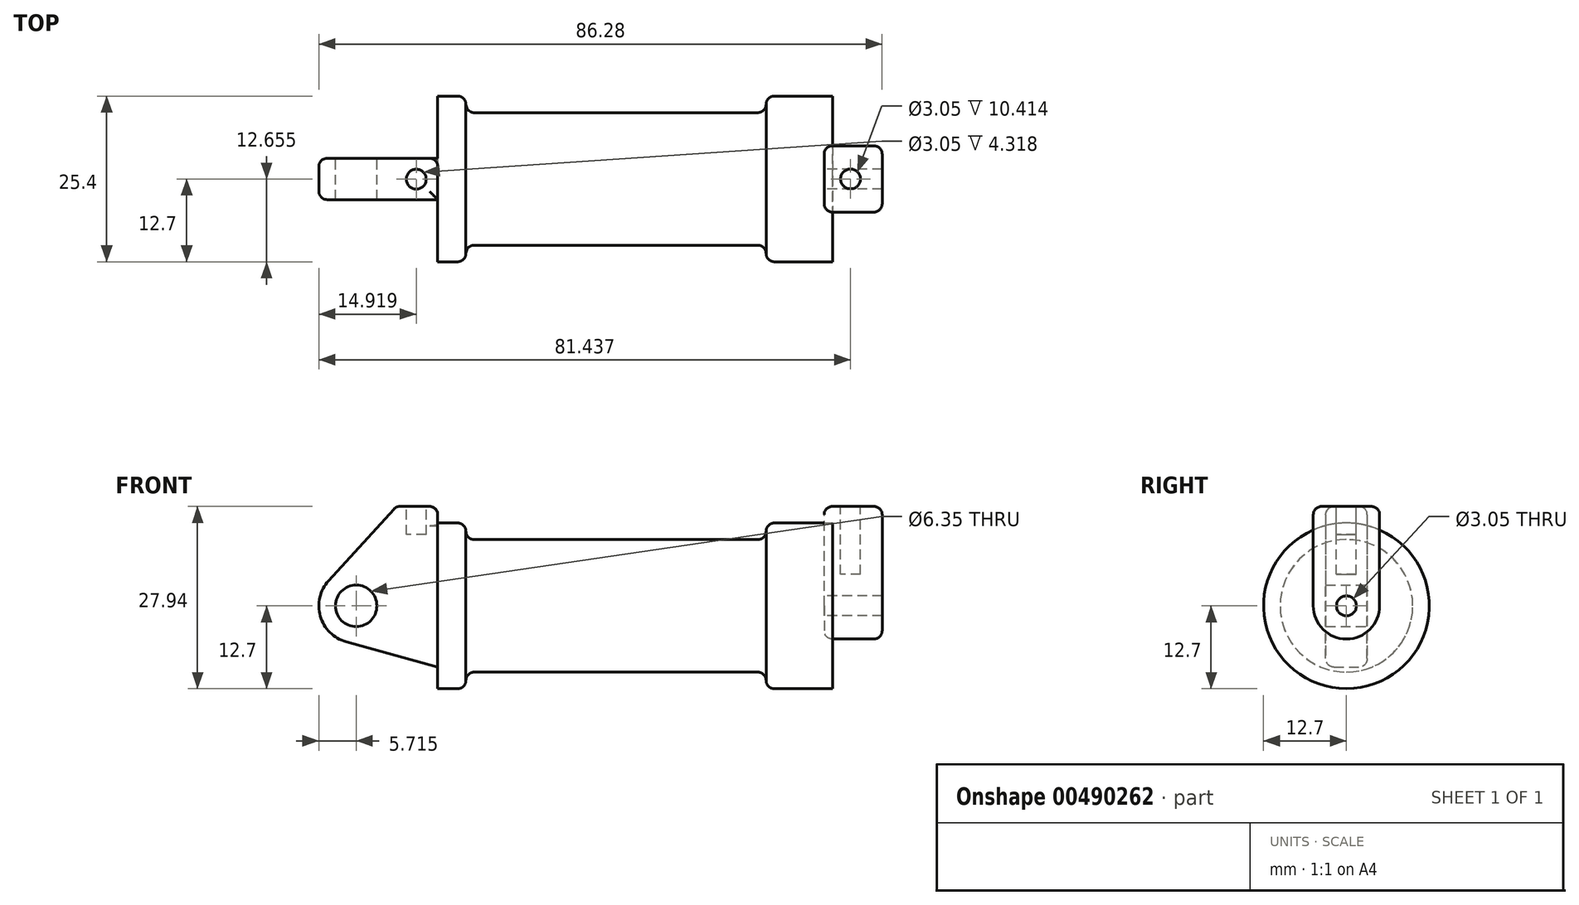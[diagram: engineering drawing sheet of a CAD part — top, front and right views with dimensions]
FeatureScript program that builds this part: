
annotation { "Feature Type Name" : "Feature", "Feature Type Description" : "" }
export const myFeature = defineFeature(function(context is Context, id is Id, definition is map)
    precondition{}
    {
        {
            var Q0;
            Q0=qCreatedBy(makeId("Front.planeOp"),FACE);
            var sketch = newSketch(context, id + "F0", { "sketchPlane" : qUnion([Q0])});
            skLineSegment(sketch, "E0", {"start": v(0, 0) * mm, "end": v(0, 12.7) * mm});
            skLineSegment(sketch, "E1", {"start": v(0, 12.7) * mm, "end": v(10.16, 12.7) * mm});
            skLineSegment(sketch, "E2", {"start": v(10.16, 12.7) * mm, "end": v(10.16, 10.16) * mm});
            skLineSegment(sketch, "E3", {"start": v(10.16, 10.16) * mm, "end": v(56.13, 10.16) * mm});
            skLineSegment(sketch, "E4", {"start": v(56.13, 10.16) * mm, "end": v(56.13, 12.7) * mm});
            skLineSegment(sketch, "E5", {"start": v(56.13, 12.7) * mm, "end": v(66.3, 12.7) * mm});
            skLineSegment(sketch, "E6", {"start": v(66.3, 12.7) * mm, "end": v(66.3, 0) * mm});
            skLineSegment(sketch, "E7", {"start": v(66.3, 0) * mm, "end": v(0, 0) * mm});
            skLineSegment(sketch, "E8", {"start": v(5.84, 15.24) * mm, "end": v(-0.5, 15.24) * mm});
            skLineSegment(sketch, "E9", {"start": v(-0.5, 15.24) * mm, "end": v(-10.88, 3.85) * mm});
            skLineSegment(sketch, "E10", {"start": v(0, 0) * mm, "end": v(-6.65, 0) * mm});
            skCircle(sketch, "E11", {"center": v(-6.65, 0) * mm, "radius": 5.72 * mm});
            skCircle(sketch, "E12", {"center": v(-6.65, 0) * mm, "radius": 3.18 * mm});
            skLineSegment(sketch, "E13", {"start": v(5.84, 15.24) * mm, "end": v(5.84, -9.4) * mm});
            skLineSegment(sketch, "E14", {"start": v(5.84, -9.4) * mm, "end": v(-8.18, -5.5) * mm});
            skSolve(sketch);
        }
        {
            var Q0;
            {var subQ0=sQuery(id+"F0.wireOp",EDGE,"E2");Q0=makeQuery(id+"F0.imprint","IMPRINT",FACE,{"disambiguationData":[TD([[makeQuery(id+"F0.imprint","IMPRINT",EDGE,{"derivedFrom":subQ0}),-1.0]])]});}
            var Q1;
            Q1=sQuery(id+"F0.wireOp",EDGE,"E7");
            var Q2;
            Q2=sQuery(id+"F0.wireOp",EDGE,"E7");
            revolve(context, id + "F1", {"entities" : qUnion([Q0]), "surfaceEntities" : qUnion([Q1]), "axis" : qUnion([Q2]), "revolveType" : RevolveType.FULL});
        }
        {
            var Q0;
            {var subQ1=sQuery(id+"F0.wireOp",EDGE,"E0");Q0=makeQuery(id+"F0.imprint","IMPRINT",FACE,{"disambiguationData":[TD([[makeQuery(id+"F0.imprint","IMPRINT",EDGE,{"derivedFrom":subQ1}),1.0]])]});}
            var Q1;
            {var subQ0=sQuery(id+"F0.wireOp",EDGE,"E0");Q1=makeQuery(id+"F0.imprint","IMPRINT",FACE,{"disambiguationData":[TD([[makeQuery(id+"F0.imprint","IMPRINT",EDGE,{"derivedFrom":subQ0}),-1.0]])]});}
            var Q2;
            {var subQ5=sQuery(id+"F0.wireOp",EDGE,"E12");Q2=makeQuery(id+"F0.imprint","IMPRINT",FACE,{"disambiguationData":[TD([[makeQuery(id+"F0.imprint","IMPRINT",EDGE,{"derivedFrom":subQ5}),-1.0]])]});}
            var Q3;
            {var subQ0=sQuery(id+"F0.wireOp",EDGE,"E14");Q3=makeQuery(id+"F0.imprint","IMPRINT",FACE,{"disambiguationData":[TD([[makeQuery(id+"F0.imprint","IMPRINT",EDGE,{"derivedFrom":subQ0}),-1.0]])]});}
            extrude(context, id + "F2", {"entities" : qUnion([Q0, Q1, Q2, Q3]), "operationType" : NewBodyOperationType.ADD, "endBound" : BoundingType.SYMMETRIC, "depth" : 6.35 * mm});
        }
        {
            var Q0;
            Q0=makeQuery(id+"F1.opRevolve","SWEPT_FACE",FACE,{"disambiguationData":[OSD([sQuery(id+"F0.wireOp",EDGE,"E6")])]});
            var sketch = newSketch(context, id + "F3", { "sketchPlane" : qUnion([Q0])});
            skCircle(sketch, "E15", {"center": v(0, 0) * mm, "radius": 5.08 * mm});
            skCircle(sketch, "E16", {"center": v(0, 0) * mm, "radius": 1.53 * mm});
            skLineSegment(sketch, "E17", {"start": v(-5.08, 0) * mm, "end": v(-5.08, 15.24) * mm});
            skLineSegment(sketch, "E18", {"start": v(-5.08, 15.24) * mm, "end": v(5.08, 15.24) * mm});
            skLineSegment(sketch, "E19", {"start": v(5.08, 15.24) * mm, "end": v(5.08, 0) * mm});
            skSolve(sketch);
        }
        {
            var Q0;
            {var subQ0=sQuery(id+"F3.wireOp",EDGE,"E18");Q0=makeQuery(id+"F3.imprint","IMPRINT",FACE,{"disambiguationData":[TD([[makeQuery(id+"F3.imprint","IMPRINT",EDGE,{"derivedFrom":subQ0}),-1.0]])]});}
            var Q1;
            {var subQ0=sQuery(id+"F3.wireOp",EDGE,"E17");var subQ1=sQuery(id+"F3.wireOp",EDGE,"E15");var subQ2=makeQuery(id+"F3.imprint","INTERSECT",VERTEX,{"derivedFrom":[subQ1,subQ0]});Q1=makeQuery(id+"F3.imprint","IMPRINT",FACE,{"disambiguationData":[TD([[makeQuery(id+"F3.imprint","IMPRINT",EDGE,{"disambiguationData":[TD([[subQ2,1.0]])],"derivedFrom":subQ1}),-1.0]])]});}
            var Q2;
            Q2=makeQuery(id+"F3.imprint","IMPRINT",FACE,{"disambiguationData":[TD([[makeQuery(id+"F3.imprint","IMPRINT",EDGE,{"derivedFrom":sQuery(id+"F3.wireOp",EDGE,"E16")}),-1.0]])]});
            extrude(context, id + "F4", {"entities" : qUnion([Q0, Q1, Q2]), "depth" : 7.62 * mm, "hasSecondDirection" : true, "secondDirectionOppositeDirection" : true, "secondDirectionDepth" : 1.27 * mm});
        }
        {
            var Q0;
            Q0=makeQuery(id+"F4.opExtrude","SWEPT_FACE",FACE,{"disambiguationData":[OSD([sQuery(id+"F3.wireOp",EDGE,"E18")])]});
            var sketch = newSketch(context, id + "F5", { "sketchPlane" : qUnion([Q0])});
            skCircle(sketch, "E20", {"center": v(69.07, 0) * mm, "radius": 1.52 * mm});
            skPoint(sketch, "E20.centerSnap0", {"position": v(73.91, 0) * mm});
            skCircle(sketch, "E21", {"center": v(2.55, -0.05) * mm, "radius": 1.52 * mm});
            skSolve(sketch);
        }
        {
            var Q0;
            Q0=makeQuery(id+"F5.imprint","IMPRINT",FACE,{"disambiguationData":[TD([[makeQuery(id+"F5.imprint","IMPRINT",EDGE,{"derivedFrom":sQuery(id+"F5.wireOp",EDGE,"E20")}),1.0]])]});
            extrude(context, id + "F6", {"entities" : qUnion([Q0]), "operationType" : NewBodyOperationType.REMOVE, "oppositeDirection" : true, "depth" : 10.4 * mm});
        }
        {
            var Q0;
            Q0=makeQuery(id+"F5.imprint","IMPRINT",FACE,{"disambiguationData":[TD([[makeQuery(id+"F5.imprint","IMPRINT",EDGE,{"derivedFrom":sQuery(id+"F5.wireOp",EDGE,"E21")}),1.0]])]});
            extrude(context, id + "F7", {"entities" : qUnion([Q0]), "operationType" : NewBodyOperationType.REMOVE, "oppositeDirection" : true, "depth" : 4.32 * mm});
        }
        {
            var Q0;
            Q0=makeQuery(id+"F1.opRevolve","SWEPT_EDGE",EDGE,{"disambiguationData":[OSD([sQuery(id+"F0.wireOp",EDGE,"E3"),sQuery(id+"F0.wireOp",EDGE,"E4")])]});
            var Q1;
            Q1=makeQuery(id+"F1.opRevolve","SWEPT_EDGE",EDGE,{"disambiguationData":[OSD([sQuery(id+"F0.wireOp",EDGE,"E1"),sQuery(id+"F0.wireOp",EDGE,"E2")])]});
            var Q2;
            Q2=makeQuery(id+"F1.opRevolve","SWEPT_EDGE",EDGE,{"disambiguationData":[OSD([sQuery(id+"F0.wireOp",EDGE,"E2"),sQuery(id+"F0.wireOp",EDGE,"E3")])]});
            var Q3;
            Q3=makeQuery(id+"F1.opRevolve","SWEPT_EDGE",EDGE,{"disambiguationData":[OSD([sQuery(id+"F0.wireOp",EDGE,"E4"),sQuery(id+"F0.wireOp",EDGE,"E5")])]});
            fillet(context, id + "F8", {"entities" : qUnion([Q0, Q1, Q2, Q3]), "radius" : 1.27 * mm, "tangentPropagation" : true, "allowEdgeOverflow" : false});
        }
        {
            var Q0;
            Q0=makeQuery(id+"F4.opExtrude","CAP_EDGE",EDGE,{"disambiguationData":[OSD([sQuery(id+"F3.wireOp",EDGE,"E18")])],"isStart":false});
            var Q1;
            Q1=makeQuery(id+"F4.opExtrude","CAP_EDGE",EDGE,{"disambiguationData":[OSD([sQuery(id+"F3.wireOp",EDGE,"E18")])],"isStart":true});
            var Q2;
            Q2=makeQuery(id+"F4.opExtrude","CAP_EDGE",EDGE,{"disambiguationData":[OSD([sQuery(id+"F3.wireOp",EDGE,"E17")])],"isStart":false});
            var Q3;
            Q3=makeQuery(id+"F4.opExtrude","SWEPT_FACE",FACE,{"disambiguationData":[OSD([sQuery(id+"F3.wireOp",EDGE,"E19")])]});
            var Q4;
            Q4=makeQuery(id+"F4.opExtrude","SWEPT_FACE",FACE,{"disambiguationData":[OSD([sQuery(id+"F3.wireOp",EDGE,"E15")])]});
            var Q5;
            Q5=makeQuery(id+"F4.opExtrude","SWEPT_FACE",FACE,{"disambiguationData":[OSD([sQuery(id+"F3.wireOp",EDGE,"E17")])]});
            fillet(context, id + "F9", {"entities" : qUnion([Q0, Q1, Q2, Q3, Q4, Q5]), "radius" : 1.27 * mm, "tangentPropagation" : true, "allowEdgeOverflow" : false});
        }
        {
            var Q0;
            Q0=makeQuery(id+"F2.opExtrude","SWEPT_EDGE",EDGE,{"disambiguationData":[OSD([sQuery(id+"F0.wireOp",EDGE,"E8"),sQuery(id+"F0.wireOp",EDGE,"E9")])]});
            var Q1;
            Q1=makeQuery(id+"F2.opExtrude","SWEPT_EDGE",EDGE,{"disambiguationData":[OSD([sQuery(id+"F0.wireOp",EDGE,"E8"),sQuery(id+"F0.wireOp",EDGE,"E13")])]});
            var Q2;
            Q2=makeQuery(id+"F2.opExtrude","CAP_EDGE",EDGE,{"disambiguationData":[OSD([sQuery(id+"F0.wireOp",EDGE,"E8")])],"isStart":true});
            var Q3;
            Q3=makeQuery(id+"F2.opExtrude","CAP_EDGE",EDGE,{"disambiguationData":[OSD([sQuery(id+"F0.wireOp",EDGE,"E8")])],"isStart":false});
            var Q4;
            Q4=makeQuery(id+"F2.opExtrude","CAP_EDGE",EDGE,{"disambiguationData":[OSD([sQuery(id+"F0.wireOp",EDGE,"E9")])],"isStart":true});
            var Q5;
            Q5=makeQuery(id+"F2.opExtrude","CAP_EDGE",EDGE,{"disambiguationData":[OSD([sQuery(id+"F0.wireOp",EDGE,"E9")])],"isStart":false});
            var Q6;
            Q6=makeQuery(id+"F2.opExtrude","CAP_EDGE",EDGE,{"disambiguationData":[OSD([sQuery(id+"F0.wireOp",EDGE,"E11")])],"isStart":true});
            var Q7;
            Q7=makeQuery(id+"F2.opExtrude","CAP_EDGE",EDGE,{"disambiguationData":[OSD([sQuery(id+"F0.wireOp",EDGE,"E14")])],"isStart":true});
            var Q8;
            {var subQ0=sQuery(id+"F0.wireOp",EDGE,"E13");Q8=makeQuery(id+"F2.boolean.opBoolean","SPLIT",EDGE,{"disambiguationData":[topologyDisambiguationEdgeConnected([makeQuery(id+"F1.opRevolve","SWEPT_FACE",FACE,{"disambiguationData":[OSD([subQ0])]})])],"derivedFrom":makeQuery(id+"F2.opExtrude","CAP_EDGE",EDGE,{"disambiguationData":[OSD([subQ0])],"isStart":true})});}
            var Q9;
            Q9=makeQuery(id+"F2.opExtrude","SWEPT_EDGE",EDGE,{"disambiguationData":[OSD([sQuery(id+"F0.wireOp",EDGE,"E13"),sQuery(id+"F0.wireOp",EDGE,"E14")])]});
            fillet(context, id + "F10", {"entities" : qUnion([Q0, Q1, Q2, Q3, Q4, Q5, Q6, Q7, Q8, Q9]), "radius" : 1.27 * mm, "tangentPropagation" : true, "allowEdgeOverflow" : false});
        }
    });
